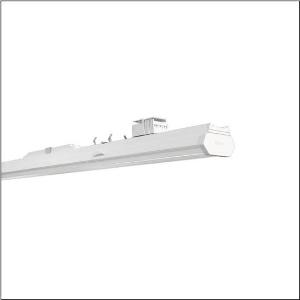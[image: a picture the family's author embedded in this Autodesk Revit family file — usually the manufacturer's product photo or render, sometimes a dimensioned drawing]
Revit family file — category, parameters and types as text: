
# Revit family: licross_11_protected_mo_51td1bdn49xgd
name_source: partatom
category: Lighting Fixtures
units: mm (PartAtom-declared; Revit-internal decimal feet)

## family parameters
Cut with Voids When Loaded = No
Host = Face
Light Source = No
Part Type = Normal
Room Calculation Point = No
Round Connector Dimension = Use Diameter
Shared = No

## types (1)
- --- (1 x LED, 1410 lm, 9.3 W, 4000K)
    Apparent Load = 9 VA
    CIE Flux Codes = 54 82 95 97 100
    Color Rendering = 80
    Color Temperature = 4000K
    Default Elevation = 1800 mm
    Description = Licross 11 Protected MO, luminaire insert, of sheet steel, galvanised, coil coated, white, length: 1.500mm, width: 90mm, height: 101mm, LED rated luminous flux: 9.370lm, light colour: 840, SDCM (Standard Deviation of Colour Matching)MacAdam ≤ 2 SDCM (initial), control gear: DALI 2 (for two DALI lines), with plug, 6-pole, with phase selection, mains connection: 220..240V, AC/DC, 0/50..60Hz, rated input power: 57W, internal wiring halogen-free, for central battery installations according to EN 60598-2-22, for emergency light function, without changeover relay, primary optical cover: cover, of PMMA, light emission: direct distribution, primary light characteristic: symmetric, protection rating (complete): IP54, insulation class (complete): insulation class I (protective earthing), certification: CE, ENEC, VDE, UKCA, protection symbol: D if used in an environment with non-conductive dust loads with corresponding accessories, impact resistance: IK06, permissible ambient temperature for indoor applications: -25..+35°C, standard: EN 60598-2-22, corresponds to IFS (International Featured Standards) requirements for safety and quality in the food industry, reducing of maximum allowable ambient temperature of 5°C with ceiling mounting, LABS conformity tested according to VDMA 24364:2018-05, The light source and the operating device comply with the requirements of the Ecodesign Regulation (EU) 2019/2020 and are replaceable in accordance with this regulation, packaging unit: 1 piece
    Height = 92 mm
    Lamp = 1 x LED
    Lamp Light Flux = 1410 lm
    Lamp Power = 9.3 W
    Lamp count = 1
    Length = 1500 mm
    Luminous efficacy = 152 lm/W
    Manufacturer = Siteco
    ModVariant = No
    Model = 51TD1BDN49XGD
    Mounting Place = Ceiling
    Mounting Type = Pendant
    Number of Poles = 1
    OnlyDefault = Yes
    Power Factor = 1
    Product Name = Licross 11 Protected MO
    Product group = luminaire insert | ceiling pendant
    ProductGroupID = 901
    Protection Class = Protection class I
    Protection Degree = IP 54
    RLX_Detail_Level = 1
    RLX_Emergency_Light_Flux = 0 lm
    RLX_Emergency_Type = 0
    RLX_Emergency_Type_DB = No
    RlxData = <blob elided: 25181 chars, md5=37481f80>
    Socket = socket
    Standby Power = 0 W
    System Light Flux = 1410 lm
    System Power = 9 W
    Type Comments = : DC mode (central or group accumulator) initial emergency light level
    Type Image = l_1256145.jpg
    URL = http://relux.com
    VarID = @adj_093217
    Voltage = 0 V
    Weight = 0.00 kg
    Width = 88 mm

## geometry (parser evidence)
native form markers: Blend x4, Sweep x12
no freeform markers — native parametric forms only
